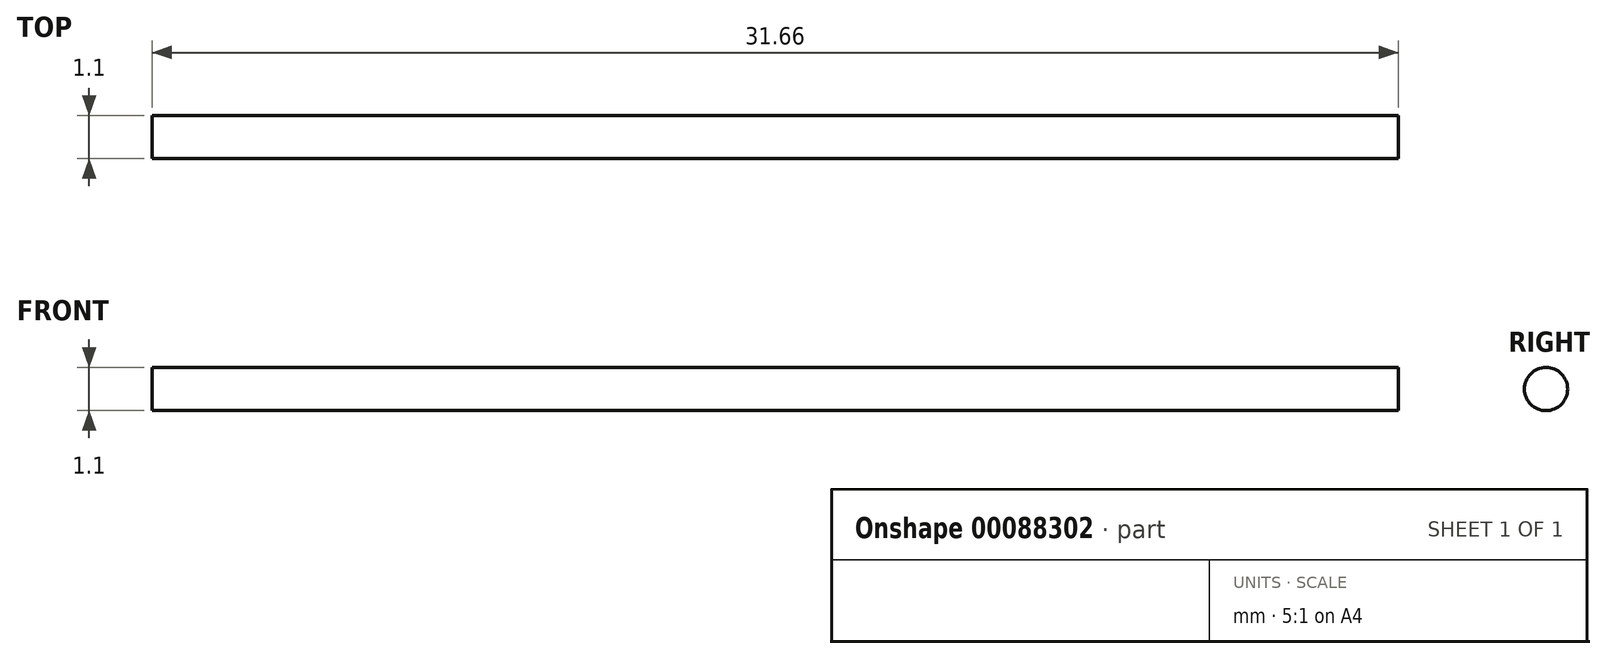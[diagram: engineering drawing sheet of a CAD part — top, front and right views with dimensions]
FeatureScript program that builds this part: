
annotation { "Feature Type Name" : "Feature", "Feature Type Description" : "" }
export const myFeature = defineFeature(function(context is Context, id is Id, definition is map)
    precondition{}
    {
        {
            var Q0;
            Q0=qCreatedBy(makeId("Right.planeOp"),FACE);
            var sketch = newSketch(context, id + "F0", { "sketchPlane" : qUnion([Q0])});
            skCircle(sketch, "E0", {"center": v(57.71, 21.23) * mm, "radius": 0.55 * mm});
            skSolve(sketch);
        }
        {
            var Q0;
            Q0 = qSketchRegion(id + "F0", true);
            extrude(context, id + "F1", {"entities" : qUnion([Q0]), "depth" : 31.66 * mm});
        }
    });
